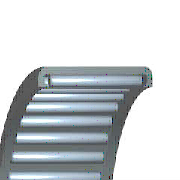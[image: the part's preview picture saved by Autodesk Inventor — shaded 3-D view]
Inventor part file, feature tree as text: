
AUTODESK INVENTOR PART (.ipt)
format: ipt  version: 2020 (Build 240168000, 168)  size: 294,400 bytes
history: native  units: mm (DEFAULTED — no unit token found)
features: sketch x1, other x1, pattern_circular x1
ambient origin geometry x8: Origin, YZ Plane, XZ Plane, XY Plane, X Axis, Y Axis, Z Axis, Center Point
bodies: Solid1 (feature_tree), Body (feature_tree)
feature tree (3):
  sketch  "Sketch"  dims[d36=90.0deg d0=1.25mm d1=0.25mm d39=90.0deg d2=200.0mm d3=360.0deg d4=0.0mm d5=0.0mm d6=1.4mm d7=0.0mm d8=12.0mm d9=16.0mm d10=13.0mm d11=14.0mm d12=1.0mm d13=1.9mm d14=7.0mm d57=0.0mm d58=0.0mm]
  other  "Roller"
  pattern_circular  "Rollers"  [2 undecoded]
note: 2 required parameter values undecoded (feature->parameter linkage not recoverable at this tier; creation-order binding heuristic only, values carry confidence <= 0.55)
